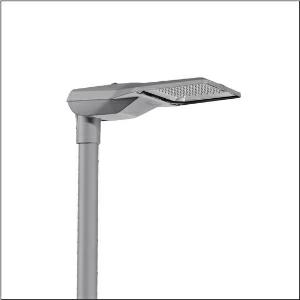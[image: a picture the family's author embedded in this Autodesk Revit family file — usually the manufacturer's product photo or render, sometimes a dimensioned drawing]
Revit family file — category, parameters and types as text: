
# Revit family: streetlight_sl_21_midi___st0_8a_5xe3c33s08lb_6676
name_source: partatom
category: Lighting Fixtures
units: mm (PartAtom-declared; Revit-internal decimal feet)

## family parameters
Cut with Voids When Loaded = No
Host = Face
Light Source = No
Part Type = Normal
Room Calculation Point = No
Round Connector Dimension = Use Diameter
Shared = No

## types (1)
- --- (1 x LED, 14340 lm, 98.3 W, 3000K)
    Apparent Load = 98 VA
    CIE Flux Codes = 38 75 97 100 100
    Color Rendering = 70
    Color Temperature = 3000K
    Default Elevation = 1800 mm
    Description = Streetlight SL 21 midi, mast luminaire, primary light control with lens, of PMMA, primary optical cover: cover, of toughened safety glass, transparent, light distribution: ST0.8a, light emission: direct distribution, primary light characteristic: asymmetric, installation type: side-entry, post-top, LED, High Power LED, rated luminous flux: 14.340lm, luminous efficacy: 146lm/W, light colour: 730, colour temperature: 3000K, control: overheat protection, constant luminous flux control, time-dependent luminous flux control, flexible luminous flux parameterisation, presetting dimming logarithmic, mains connection: 230..240V, AC, 50/60Hz, start of lifetime: 98W, end of service life: 101W, reduction: 45W, luminaire housing, of diecast aluminium, powder-coated, Siteco® metallic grey (DB 702S), corrosivity category C5 mid according to DIN EN ISO 12944, please order mast flange separately, inclination adjustable: 0°, 5°, 10°, 15°, sealing non-destructively replaceable, multi-level sealing system, length: 644mm, width: 335mm, height: 110mm, mast flange for spigot size: 42mm (side-entry): 5XC10008XM4, 60/48mm (side-entry/post-top): 5XC10108XM2, 76/60mm (side-entry/post-top): 5XC10108XM1, Smart Interface above, protection rating (complete): IP66, insulation class (complete): insulation class II (safety insulation), certification: CE, ENEC, ENEC+, VDE, impact resistance: IK09, permissible operating ambient temperature for outdoor applications: -40..+50°C, standard-compliant lighting for roads and squares, packaging unit: 1 piece

Light Distribution: ST0.8a
    Height = 111 mm
    Lamp = 1 x LED
    Lamp Light Flux = 14340 lm
    Lamp Power = 98.3 W
    Lamp count = 1
    Length = 644 mm
    Luminous efficacy = 146 lm/W
    Manufacturer = Siteco
    ModVariant = No
    Model = 5XE3C33S08LB
    Number of Poles = 1
    OnlyDefault = Yes
    Power Factor = 1
    Product Name = Streetlight SL 21 midi | ST0.8a
    Product group = mast luminaire | pylon top
    ProductGroupID = 6100
    Protection Class = Protection class II
    Protection Degree = IP 66
    RLX_Detail_Level = 1
    RLX_Emergency_Light_Flux = 0 lm
    RLX_Emergency_Type = 0
    RLX_Emergency_Type_DB = No
    RlxData = <blob elided: 90261 chars, md5=3f868d35>
    Socket = socket
    Standby Power = 0 W
    System Light Flux = 14340 lm
    System Power = 98 W
    Type Comments = factory setting: luminous flux: 100 % | dim-lin: 254 | 1020 mA
    Type Image = l_1004302.jpg
    URL = http://relux.com
    VarID = @adj_137935
    Voltage = 0 V
    Weight = 0.00 kg
    Width = 336 mm

## geometry (parser evidence)
native form markers: Blend x4, Sweep x11
no freeform markers — native parametric forms only
